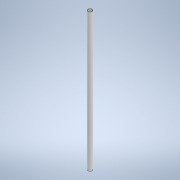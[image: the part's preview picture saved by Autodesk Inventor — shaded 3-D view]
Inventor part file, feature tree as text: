
AUTODESK INVENTOR PART (.ipt)
format: ipt  version: 2022 (Build 260153000, 153)  size: 151,040 bytes
history: native  units: mm
features: extrude x1, sketch x1
ambient origin geometry x8: Origin, YZ Plane, XZ Plane, XY Plane, X Axis, Y Axis, Z Axis, Center Point
bodies: Body1 (feature_tree)
feature tree (2):
  extrude  "Extrusion5"  Depth=500.0mm
  sketch  "Sketch2"  dims[d31=34.456mm d91=15.0mm d92=13.0mm d93=500.0mm d94=0.0mm]
